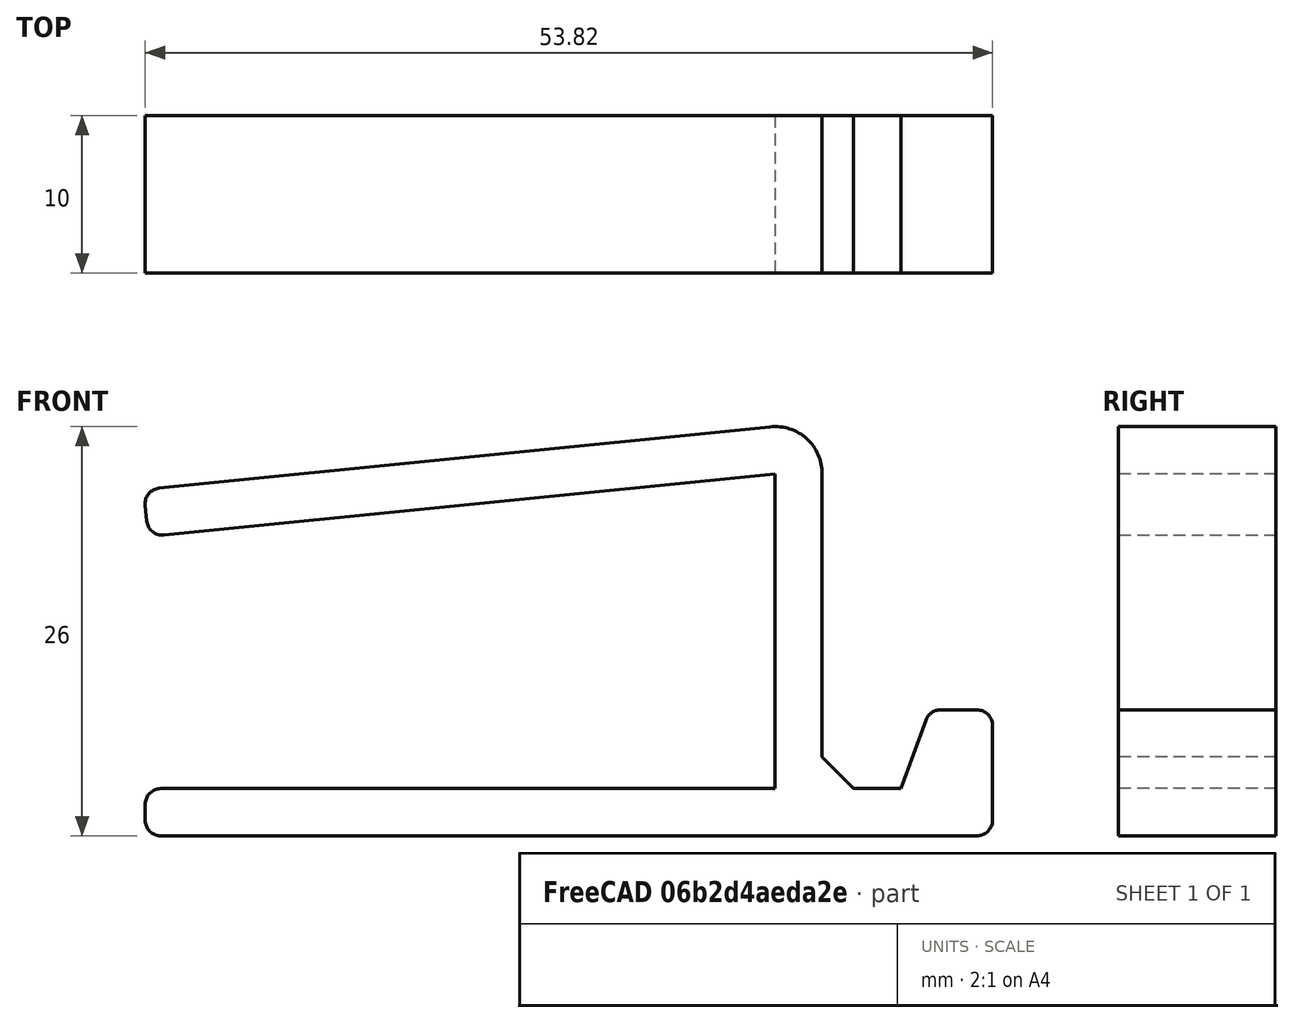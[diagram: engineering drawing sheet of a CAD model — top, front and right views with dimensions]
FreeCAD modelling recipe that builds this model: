
FCSTD DOCUMENT  (FreeCAD 0.17R13217 (Git))
Label: 08-01-gancho-mesa
License: All rights reserved
LicenseURL: http://en.wikipedia.org/wiki/All_rights_reserved
objects: TechDraw::DrawViewDimension×9, PartDesign::Fillet×2, TechDraw::DrawProjGroupItem×2, Sketcher::SketchObject×1, PartDesign::Pad×1, PartDesign::Chamfer×1, PartDesign::Body×1, TechDraw::DrawSVGTemplate×1, TechDraw::DrawProjGroup×1, TechDraw::DrawViewPart×1, TechDraw::DrawViewAnnotation×1, TechDraw::DrawPage×1
note: 7 computed .brp shape members not serialized (recipe doc carries the construction recipe); baked Part::Feature solids carry a one-line shape summary decoded from their .brp

FEATURE [Sketcher::SketchObject] Sketch
  MapMode = 5
  Placement = pos=(0,0,0) rot=(1,0,0;1.5708rad)
  Support = -> [XZ_Plane]
  sketch-geometry (14):
    g0: LineSegment StartX=-43.0995 StartY=8.82665 StartZ=0 EndX=0 EndY=13.1583 EndZ=0
    g1: LineSegment StartX=0 StartY=-13.1583 StartZ=0 EndX=-43 EndY=-13.1583 EndZ=0
    g2: LineSegment StartX=-43 StartY=-13.1583 StartZ=0 EndX=-43 EndY=-10.1583 EndZ=0
    g3: LineSegment StartX=-43 StartY=-10.1583 StartZ=0 EndX=-3 EndY=-10.1583 EndZ=0
    g4: LineSegment StartX=-3 StartY=-10.1583 StartZ=0 EndX=-3 EndY=9.84169 EndZ=0
    g5: LineSegment StartX=-3 StartY=9.84169 StartZ=0 EndX=-42.7995 EndY=5.84169 EndZ=0
    g6: LineSegment StartX=-42.7995 StartY=5.84169 StartZ=0 EndX=-43.0995 EndY=8.82665 EndZ=0
    g7: LineSegment StartX=0 StartY=-13.1583 StartZ=0 EndX=10.8199 EndY=-13.1583 EndZ=0
    g8: LineSegment StartX=10.8199 StartY=-13.1583 StartZ=0 EndX=10.8199 EndY=-5.15831 EndZ=0
    g9: LineSegment StartX=10.8199 StartY=-5.15831 StartZ=0 EndX=6.81985 EndY=-5.15831 EndZ=0
    g10: LineSegment StartX=6.81985 StartY=-5.15831 StartZ=0 EndX=5 EndY=-10.1583 EndZ=0
    g11: LineSegment StartX=5 StartY=-10.1583 StartZ=0 EndX=0 EndY=-10.1583 EndZ=0
    g12: LineSegment StartX=0 StartY=-10.1583 StartZ=0 EndX=0 EndY=13.1583 EndZ=0
    g13: LineSegment [constr] StartX=-3 StartY=-10.1583 StartZ=0 EndX=0 EndY=-13.1583 EndZ=0
  constraints (40):
    c: Horizontal(g1)
    c: PointOnObject(g1,g-2)
    c: Symmetric(g0,g1,g-1)
    c: Coincident(g1,g2)
    c: Coincident(g2,g3)
    c: Horizontal(g3)
    c: Coincident(g3,g4)
    c: Vertical(g4)
    c: Coincident(g4,g5)
    c: Coincident(g5,g6)
    c: Coincident(g6,g0)
    c: Vertical(g2)
    c: DistanceY(g2,g2) = 3
    c: DistanceX(g3,g3) = 40
    c: DistanceY(g4,g4) = 20
    c: Equal(g6,g2)
    c: Perpendicular(g6,g5)
    c: Parallel(g0,g5)
    c: Equal(g3,g5)
    c: DistanceY(g5,g4) = 4
    c: Horizontal(g7)
    c: Coincident(g7,g8)
    c: Vertical(g8)
    c: Coincident(g8,g9)
    c: Coincident(g9,g10)
    c: Coincident(g10,g11)
    c: Horizontal(g11)
    c: Coincident(g11,g12)
    c: Vertical(g12)
    c: Coincident(g12,g0)
    c: PointOnObject(g11,g3)
    c: Coincident(g13,g3)
    c: Coincident(g13,g7)
    c: Angle(g-2,g13) = 0.785398
    c: Coincident(g7,g1)
    c: DistanceX(g11,g11) = 5
    c: Horizontal(g9)
    c: DistanceY(g10,g9) = 5
    c: DistanceX(g9,g9) = 4
    c: Angle(g10,g12) = 0.349066
FEATURE [PartDesign::Pad] Pad
  Length = 10
  Length2 = 100
  Midplane = true
  Placement = pos=(0,0,0) rot=(1,0,0;1.5708rad)
  Profile = -> Sketch
  Refine = true
  Type = 0
FEATURE [PartDesign::Fillet] Fillet
  Base = -> Pad [Edge17]
  BaseFeature = -> Pad
  Placement = pos=(0,0,0) rot=(1,0,0;1.5708rad)
  Radius = 3
FEATURE [PartDesign::Chamfer] Chamfer
  Base = -> Fillet [Edge31]
  BaseFeature = -> Fillet
  Placement = pos=(0,0,0) rot=(1,0,0;1.5708rad)
  Size = 2
FEATURE [PartDesign::Fillet] Fillet001
  Base = -> Chamfer [Edge28,Edge24,Edge40,Edge38,Edge30,Edge26,Edge34]
  BaseFeature = -> Chamfer
  Placement = pos=(0,0,0) rot=(1,0,0;1.5708rad)
  Radius = 1
FEATURE [PartDesign::Body] Body
  Group = -> [Sketch,Pad,Fillet,Chamfer,Fillet001]
  Origin = -> Origin
  Tip = -> Fillet001
FEATURE [TechDraw::DrawSVGTemplate] Template
  EditableTexts = Designed_by_Name=Designed by Name; Drawing_number=Drawing number; FC-Date=Date; FC-SC=Scale; FC-SH=Sheet; FC-Title=Title; Subtitle=Subtitle; Weight=Weight
  Height = 210
  Orientation = 1
  Width = 297
FEATURE [TechDraw::DrawProjGroupItem] ProjItem  label="Front"
  ArcCenterMarks = true
  CenterScale = 2
  CoarseView = false
  Direction = (0,-1,0)
  ExtraWidth = 1.4
  Focus = 100
  HardHidden = false
  HiddenWidth = 0.35
  HorizCenterLine = false
  IsoCount = 0
  IsoHidden = false
  IsoVisible = false
  IsoWidth = 0.5
  KeepLabel = false
  LineWidth = 0.7
  LockPosition = false
  Perspective = false
  Rotation = 0
  RotationVector = (1,0,0)
  ScaleType = 0
  SeamHidden = false
  SeamVisible = false
  ShowSectionLine = true
  SmoothHidden = false
  SmoothVisible = false
  Source = -> [Fillet001]
  Type = 0
  VertCenterLine = false
  X = 0
  Y = 0
FEATURE [TechDraw::DrawProjGroupItem] ProjItem001  label="Top"
  ArcCenterMarks = true
  CenterScale = 2
  CoarseView = false
  Direction = (0,0,1)
  ExtraWidth = 1.4
  Focus = 100
  HardHidden = false
  HiddenWidth = 0.35
  HorizCenterLine = false
  IsoCount = 0
  IsoHidden = false
  IsoVisible = false
  IsoWidth = 0.5
  KeepLabel = false
  LineWidth = 0.7
  LockPosition = false
  Perspective = false
  Rotation = 0
  RotationVector = (1,0,0)
  ScaleType = 0
  SeamHidden = false
  SeamVisible = false
  ShowSectionLine = true
  SmoothHidden = false
  SmoothVisible = false
  Source = -> [Fillet001]
  Type = 4
  VertCenterLine = false
  X = 0
  Y = -67
FEATURE [TechDraw::DrawProjGroup] ProjGroup
  Anchor = -> ProjItem
  AutoDistribute = true
  CubeDirs = (1) [(0,0,0)]
  CubeRotations = (1) [(0,0,0)]
  KeepLabel = false
  LockPosition = false
  ProjectionType = 0
  Rotation = 0
  Scale = 2
  ScaleType = 0
  Source = -> [Fillet001]
  Views = -> [ProjItem,ProjItem001]
  X = 77.8407
  Y = 156.153
  spacingX = 15
  spacingY = 15
FEATURE [TechDraw::DrawViewPart] View
  ArcCenterMarks = true
  CenterScale = 2
  CoarseView = false
  Direction = (1,1,1)
  ExtraWidth = 1.4
  Focus = 100
  HardHidden = false
  HiddenWidth = 0.35
  HorizCenterLine = false
  IsoCount = 0
  IsoHidden = false
  IsoVisible = false
  IsoWidth = 0.5
  KeepLabel = false
  LineWidth = 0.7
  LockPosition = false
  Perspective = false
  Rotation = 0
  Scale = 2
  ScaleType = 0
  SeamHidden = false
  SeamVisible = false
  ShowSectionLine = true
  SmoothHidden = false
  SmoothVisible = false
  Source = -> [Fillet001]
  VertCenterLine = false
  X = 214.31
  Y = 141.232
FEATURE [TechDraw::DrawViewDimension] Dimension
  Font = osifont
  Fontsize = 3.5
  FormatSpec = %.2f
  KeepLabel = false
  LineWidth = 0.5
  LockPosition = false
  MeasureType = 1
  References2D = -> [ProjItem]
  Rotation = 0
  Scale = 2
  ScaleType = 0
  Type = 1
  X = -4.76882
  Y = 9.56264
FEATURE [TechDraw::DrawViewDimension] Dimension001
  Font = osifont
  Fontsize = 3.5
  FormatSpec = %.2f
  KeepLabel = false
  LineWidth = 0.5
  LockPosition = false
  MeasureType = 1
  References2D = -> [ProjItem]
  Rotation = 0
  Scale = 2
  ScaleType = 0
  Type = 2
  X = 35.0005
  Y = 1.25002
FEATURE [TechDraw::DrawViewDimension] Dimension002
  Font = osifont
  Fontsize = 3.5
  FormatSpec = %.2f
  KeepLabel = false
  LineWidth = 0.5
  LockPosition = false
  MeasureType = 1
  References2D = -> [ProjItem]
  Rotation = 0
  Scale = 2
  ScaleType = 0
  Type = 2
  X = -63.1697
  Y = 7.86887
FEATURE [TechDraw::DrawViewDimension] Dimension003
  Font = osifont
  Fontsize = 3.5
  FormatSpec = %.2f
  KeepLabel = false
  LineWidth = 0.5
  LockPosition = false
  MeasureType = 1
  References2D = -> [ProjItem001]
  Rotation = 0
  Scale = 2
  ScaleType = 0
  Type = 2
  X = 63.0662
  Y = -0.061818
FEATURE [TechDraw::DrawViewDimension] Dimension004
  Font = osifont
  Fontsize = 3.5
  FormatSpec = %.2f
  KeepLabel = false
  LineWidth = 0.5
  LockPosition = false
  MeasureType = 1
  References2D = -> [ProjItem]
  Rotation = 0
  Scale = 2
  ScaleType = 0
  Type = 1
  X = -4.92958
  Y = 33.7676
FEATURE [TechDraw::DrawViewDimension] Dimension005
  Font = osifont
  Fontsize = 3.5
  FormatSpec = %.2f
  KeepLabel = false
  LineWidth = 0.5
  LockPosition = false
  MeasureType = 1
  References2D = -> [ProjItem]
  Rotation = 0
  Scale = 2
  ScaleType = 0
  Type = 2
  X = 64.8239
  Y = -0.246479
FEATURE [TechDraw::DrawViewDimension] Dimension006
  Font = osifont
  Fontsize = 3.5
  FormatSpec = %.2f
  KeepLabel = false
  LineWidth = 0.5
  LockPosition = false
  MeasureType = 1
  References2D = -> [ProjItem]
  Rotation = 0
  Scale = 2
  ScaleType = 0
  Type = 4
  X = 56.9366
  Y = -35.2465
FEATURE [TechDraw::DrawViewDimension] Dimension007
  Font = osifont
  Fontsize = 3.5
  FormatSpec = %.2f
  KeepLabel = false
  LineWidth = 0.5
  LockPosition = false
  MeasureType = 1
  References2D = -> [ProjItem]
  Rotation = 0
  Scale = 2
  ScaleType = 0
  Type = 4
  X = -49.8445
  Y = -30.7817
FEATURE [TechDraw::DrawViewDimension] Dimension008
  Font = osifont
  Fontsize = 3.5
  FormatSpec = %.2f
  KeepLabel = false
  LineWidth = 0.5
  LockPosition = false
  MeasureType = 1
  References2D = -> [ProjItem]
  Rotation = 0
  Scale = 2
  ScaleType = 0
  Type = 2
  X = 9.3662
  Y = -3.4507
FEATURE [TechDraw::DrawViewAnnotation] Annotation
  Font = osifont
  KeepLabel = false
  LineSpace = 80
  LockPosition = false
  MaxWidth = -1
  Rotation = 0
  Scale = 2
  ScaleType = 0
  Text = Gancho para mesa
  TextSize = 8
  TextStyle = 0
  X = 77.2189
  Y = 44.5191
FEATURE [TechDraw::DrawPage] Page
  KeepUpdated = true
  ProjectionType = 0
  Scale = 2
  Template = -> Template
  Views = -> [ProjGroup,View,Dimension,Dimension001,Dimension002,Dimension003,Dimension004,Dimension005,Dimension006,Dimension007,Dimension008,Annotation]
